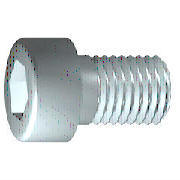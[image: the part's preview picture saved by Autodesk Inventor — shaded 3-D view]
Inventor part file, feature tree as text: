
AUTODESK INVENTOR PART (.ipt)
format: ipt  version: 2023.3 (Build 273359000, 359)  size: 189,952 bytes
history: native  units: mm (DEFAULTED — no unit token found)
features: sketch x2, other x1, extrude x1, plane x1, fillet x1
ambient origin geometry x7: Origin, YZ Plane, XY Plane, X Axis, Y Axis, Z Axis, Center Point
bodies: Solid1 (feature_tree)
feature tree (6):
  other  "Körper"
  extrude  "Loch"  Depth=1.6mm
  plane  "Work Plane1"
  fillet  "Fillet2"  Radius=1.6mm
  sketch  "Skizze1"  dims[d1=7.125mm d2=0.214807mm d3=1.6mm]
  sketch  "Skizze2"  dims[d4=0.7mm d5=60.0deg d6=1.6mm d7=1.6mm d8=1.732051mm d9=3.0mm d10=90.0deg d11=10.0mm d12=0.0mm d13=7.125mm d14=0.0mm d15=0.214707mm d16=0.214707mm d17=0.16mm d19=0.0mm d26=8.0mm d27=45.0deg d28=0.0mm d29=0.0mm d30=0.1mm]
